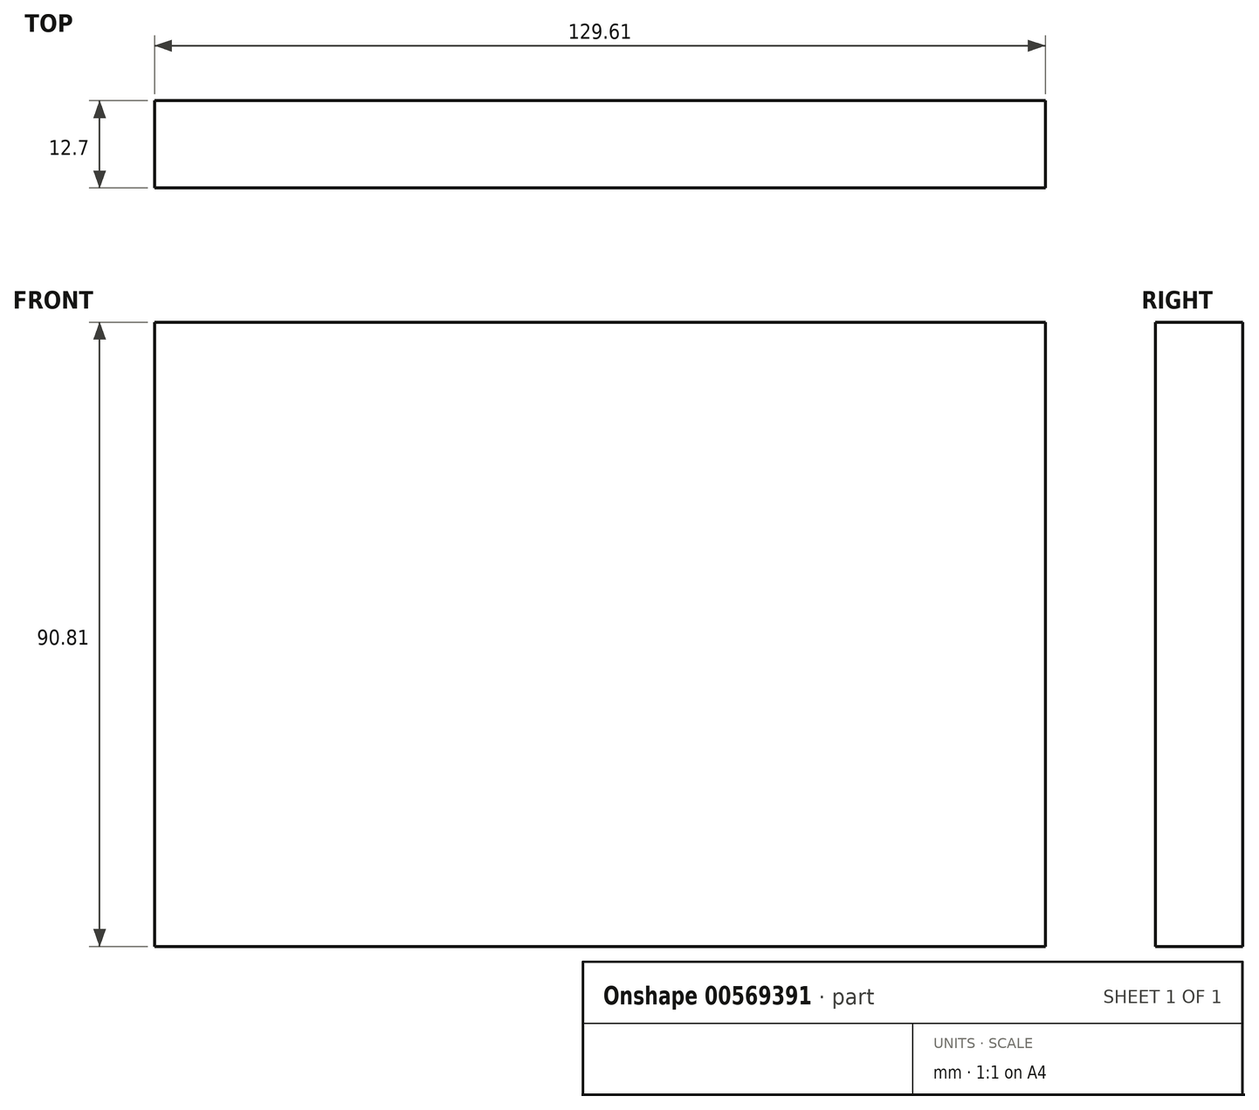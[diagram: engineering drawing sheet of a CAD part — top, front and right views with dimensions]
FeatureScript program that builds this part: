
annotation { "Feature Type Name" : "Feature", "Feature Type Description" : "" }
export const myFeature = defineFeature(function(context is Context, id is Id, definition is map)
    precondition{}
    {
        {
            var Q0;
            Q0=qCreatedBy(makeId("Front.planeOp"),FACE);
            var sketch = newSketch(context, id + "F0", { "sketchPlane" : qUnion([Q0])});
            skLineSegment(sketch, "E0.bottom", {"start": v(-59.3, 36.53) * mm, "end": v(70.31, 36.53) * mm});
            skLineSegment(sketch, "E0.top", {"start": v(-59.3, -54.28) * mm, "end": v(70.31, -54.28) * mm});
            skLineSegment(sketch, "E0.left", {"start": v(-59.3, 36.53) * mm, "end": v(-59.3, -54.28) * mm});
            skLineSegment(sketch, "E0.right", {"start": v(70.31, 36.53) * mm, "end": v(70.31, -54.28) * mm});
            skSolve(sketch);
        }
        {
            var Q0;
            Q0=makeQuery(id+"F0.imprint","IMPRINT",FACE,{"disambiguationData":[TD([[makeQuery(id+"F0.imprint","IMPRINT",EDGE,{"derivedFrom":sQuery(id+"F0.wireOp",EDGE,"E0.bottom")}),-1.0]])]});
            extrude(context, id + "F1", {"entities" : qUnion([Q0]), "depth" : 12.7 * mm, "offsetDistance" : 25.4 * mm});
        }
    });
